# Revit family: XB-EFA-82
name_source: partatom
category: Mechanical Equipment
revit_build: Autodesk Revit 2015 (Build: 20140606_1530(x64)
units: mm (PartAtom-declared; Revit-internal decimal feet)

## types (2) — shared parameters
Apparent Load = 0 VA
Classification.Uniclass.Pr.Description = Centrifugal fans
Classification.Uniclass.Pr.Number = Pr_65_67_29_12
Condensate Drain Connection Diameter = 0 mm
Condensate Drain Connection Radius = 0 mm
Description = EFA Heat Recovery Unit (Left Handed)
Duct Connection Height = 140 mm  [stored 0.459318 ft]
Duct Connection Width = 1240 mm  [stored 4.06824 ft]
Electrical Phase = 1
Fax Number = +44(0)2920-858-222
Full Load Current = 0 A
Height = 425 mm  [stored 1.39436 ft]
IFCExportAs = IfcAirToAirHeatRecoveryType
Length = 1600 mm  [stored 5.24934 ft]
Manufacturer = Nuaire
Manufacturer Name = Nuaire
Maximum Ambient Temperature = 40 °C
Nominal Motor Rating = 0.000 kW
Number of Motor Poles = 4
OmniClass Number = 23-33 31 19 13
OmniClass Title = Centrifugal fans
Postcode = CF83 1NA
Revit Family Last Revised = 24/10/18
Starting Current = 0 A
Telephone Number = +44(0)2920-858-200
URL = http://www.nuaire.co.uk
Unit Description = EFA Heat Recovery Unit (Left Handed)
Voltage = 230 V
Warranty Period = 3 Years
Weatherproof or Internal Only = Internal
Weight = 0.00 kg
Width = 1596 mm  [stored 5.23622 ft]
zero-valued in all types: Nominal Motor Speed (rpm)

## per-type parameters (varying)
| type | Left Handed | Number of Connection Poles | Panel Offset | Right Handed | ctrl_offset | duct_angle |
| XB-EFA-8L | Yes | 1 | 455 mm | No | 50 mm  [stored 0.164042 ft] | 90.00° |
| XB-EFA-8R | No | 2 | 1145 mm | Yes | 1296 mm  [stored 4.25197 ft] | 270.00° |

note: column(s) folded — value = type name in every type: Model, Nuaire Model Code

note: [stored X ft] marks values corroborated as IEEE doubles in the binary element streams (Revit-internal decimal feet)

## geometry (parser evidence)
native form markers: Blend x2, Sweep x19
no freeform markers — native parametric forms only
